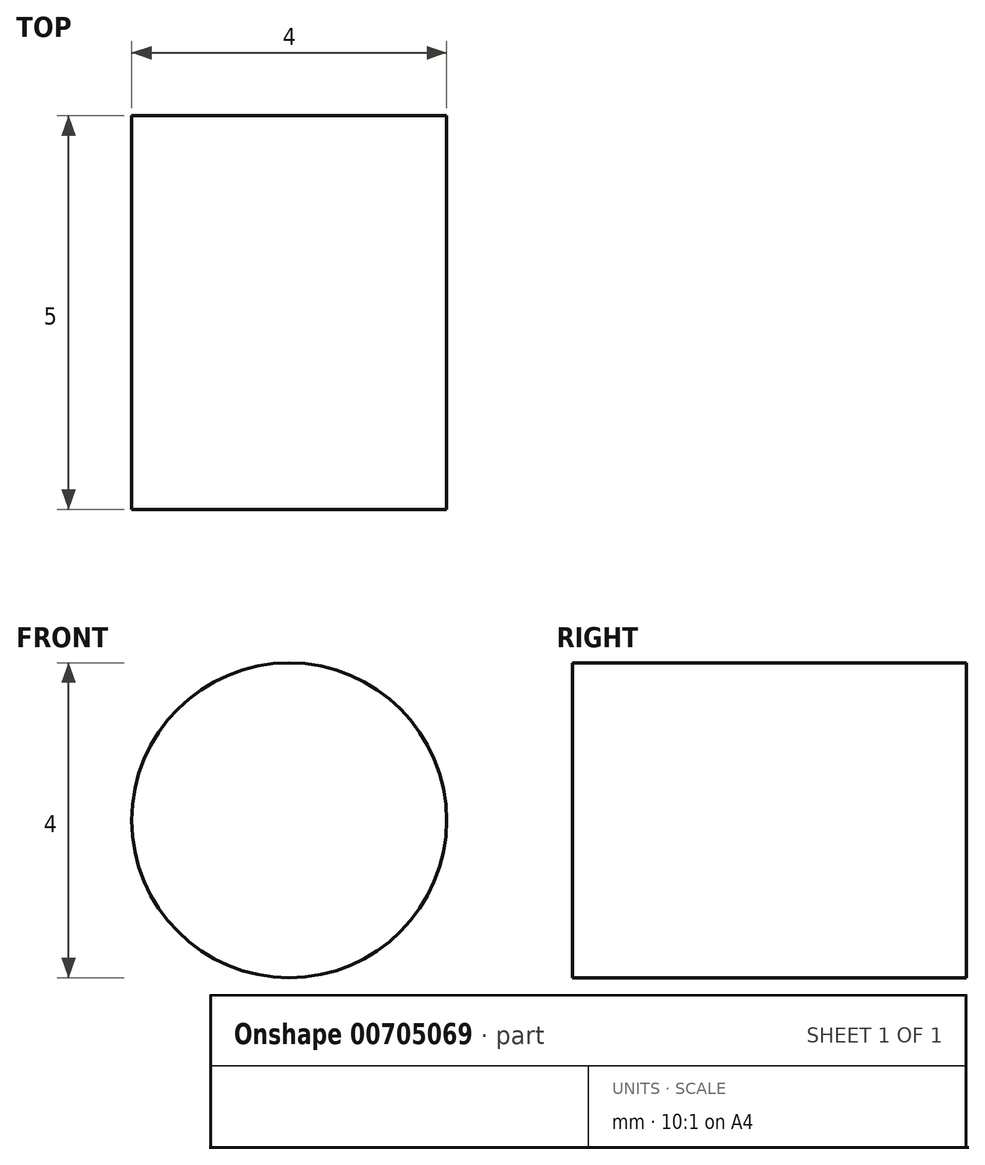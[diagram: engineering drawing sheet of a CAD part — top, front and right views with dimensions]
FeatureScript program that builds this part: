
annotation { "Feature Type Name" : "Feature", "Feature Type Description" : "" }
export const myFeature = defineFeature(function(context is Context, id is Id, definition is map)
    precondition{}
    {
        {
            var Q0;
            Q0=qCreatedBy(makeId("Front.planeOp"),FACE);
            var sketch = newSketch(context, id + "F0", { "sketchPlane" : qUnion([Q0])});
            skCircle(sketch, "E0", {"center": v(0, 0) * mm, "radius": 2 * mm});
            skSolve(sketch);
        }
        {
            var Q0;
            Q0=makeQuery(id+"F0.imprint","IMPRINT",FACE,{"disambiguationData":[TD([[makeQuery(id+"F0.imprint","IMPRINT",EDGE,{"derivedFrom":sQuery(id+"F0.wireOp",EDGE,"E0")}),1.0]])]});
            extrude(context, id + "F1", {"entities" : qUnion([Q0]), "depth" : 5 * mm, "offsetDistance" : 25 * mm});
        }
    });
